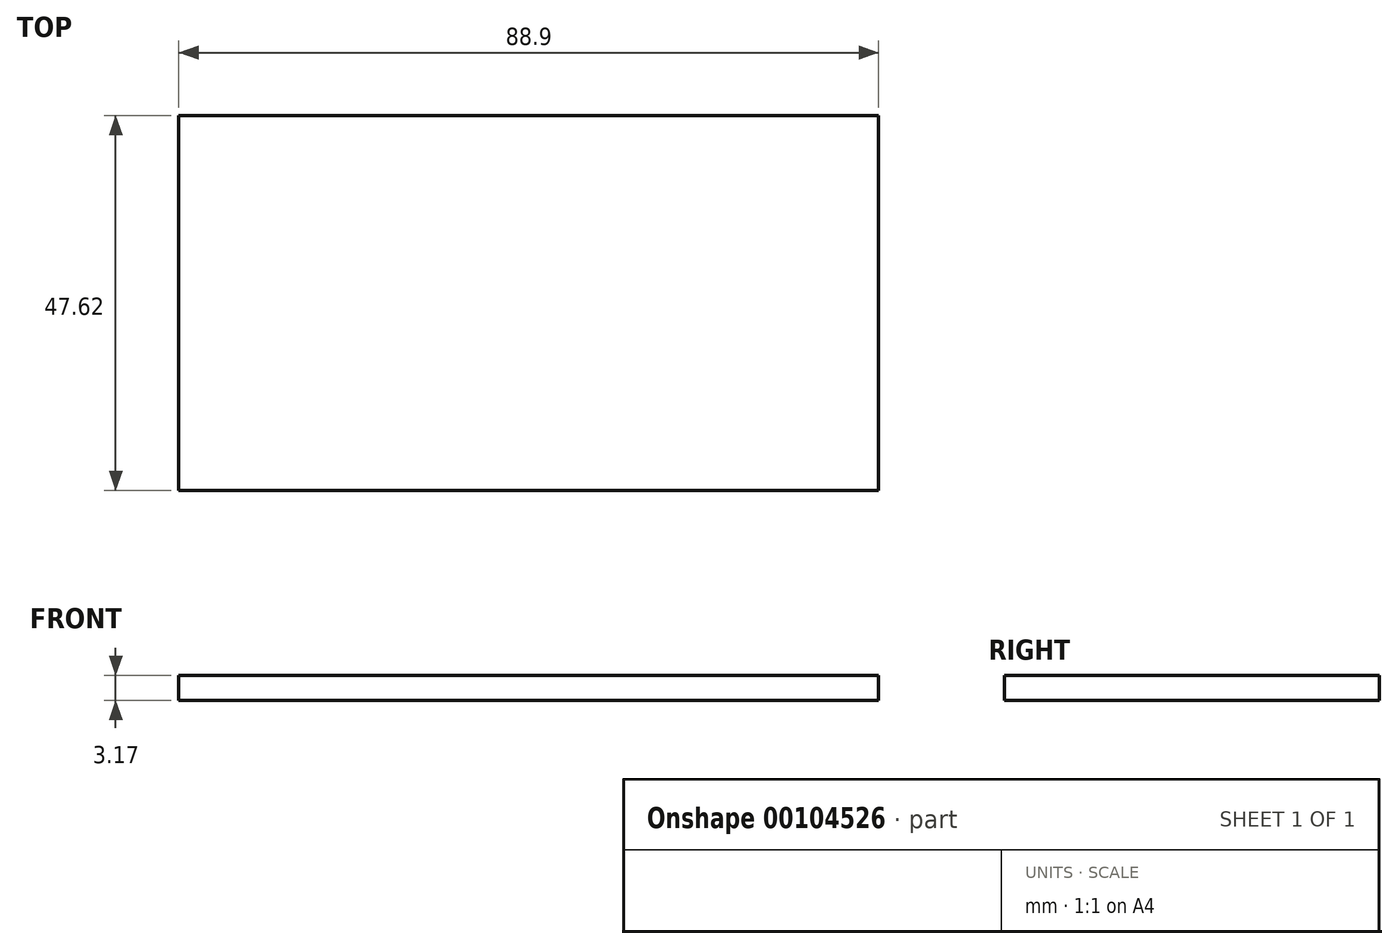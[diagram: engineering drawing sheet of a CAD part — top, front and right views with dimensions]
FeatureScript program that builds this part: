
annotation { "Feature Type Name" : "Feature", "Feature Type Description" : "" }
export const myFeature = defineFeature(function(context is Context, id is Id, definition is map)
    precondition{}
    {
        {
            var Q0;
            Q0=qCreatedBy(makeId("Top.planeOp"),FACE);
            var sketch = newSketch(context, id + "F0", { "sketchPlane" : qUnion([Q0])});
            skLineSegment(sketch, "E0.bottom", {"start": v(0, 0) * mm, "end": v(88.9, 0) * mm});
            skLineSegment(sketch, "E0.top", {"start": v(0, 47.63) * mm, "end": v(88.9, 47.63) * mm});
            skLineSegment(sketch, "E0.left", {"start": v(0, 0) * mm, "end": v(0, 47.63) * mm});
            skLineSegment(sketch, "E0.right", {"start": v(88.9, 0) * mm, "end": v(88.9, 47.63) * mm});
            skSolve(sketch);
        }
        {
            var Q0;
            Q0 = qSketchRegion(id + "F0", true);
            extrude(context, id + "F1", {"entities" : qUnion([Q0]), "depth" : 3.17 * mm});
        }
    });
